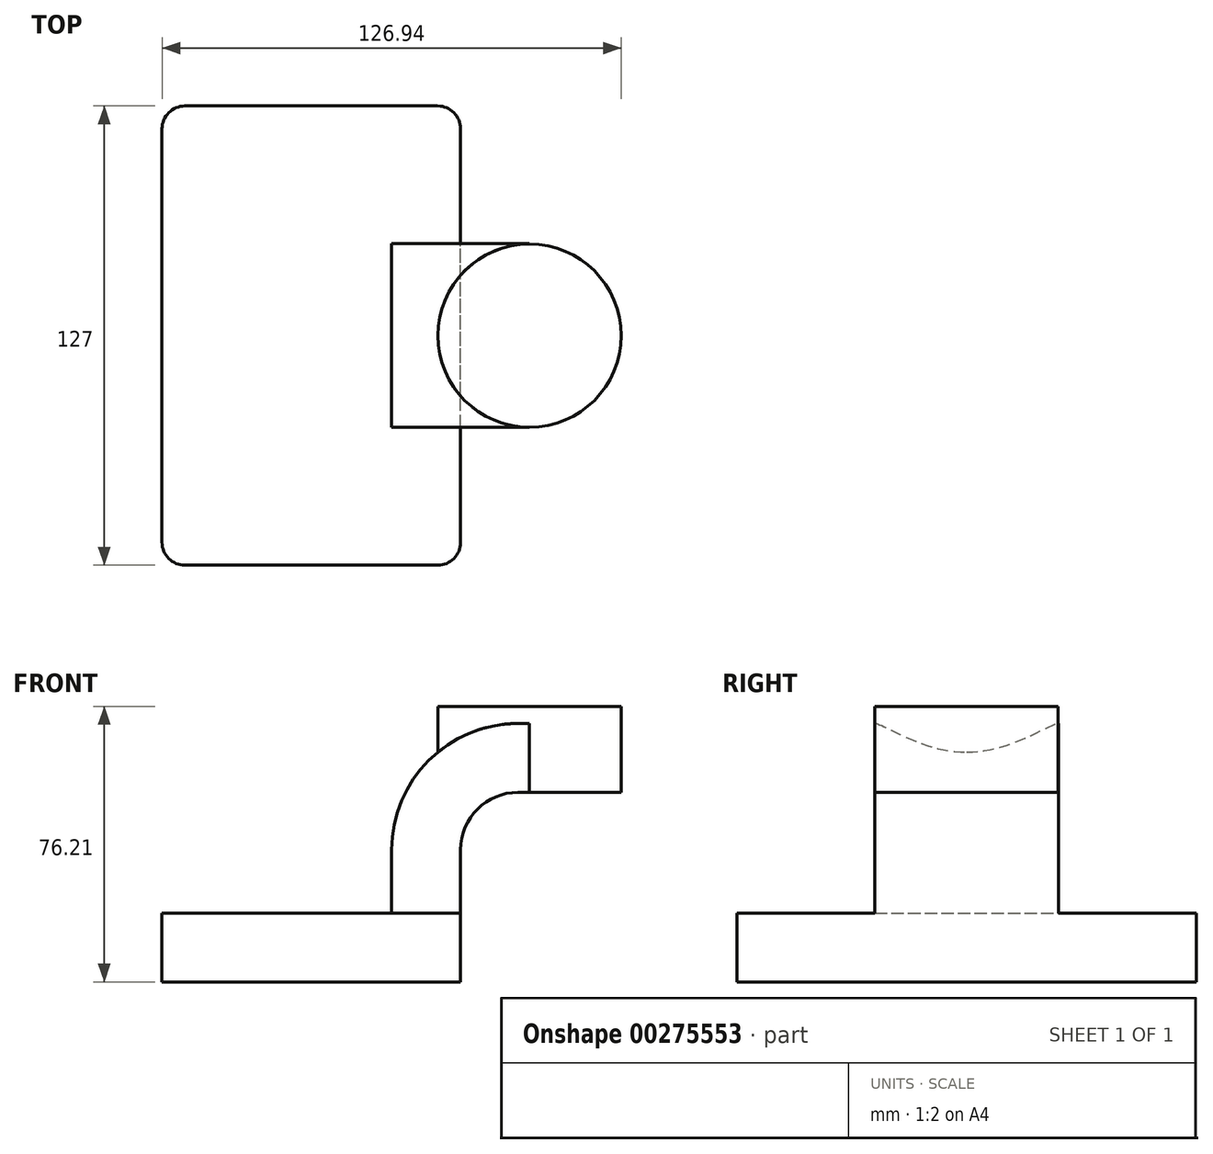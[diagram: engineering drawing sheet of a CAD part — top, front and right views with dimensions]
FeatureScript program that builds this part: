
annotation { "Feature Type Name" : "Feature", "Feature Type Description" : "" }
export const myFeature = defineFeature(function(context is Context, id is Id, definition is map)
    precondition{}
    {
        {
            var Q0;
            Q0=qCreatedBy(makeId("Front.planeOp"),FACE);
            var sketch = newSketch(context, id + "F0", { "sketchPlane" : qUnion([Q0])});
            skLineSegment(sketch, "E0.bottom", {"start": v(41.28, -9.52) * mm, "end": v(-41.28, -9.53) * mm});
            skLineSegment(sketch, "E0.top", {"start": v(41.28, 9.53) * mm, "end": v(-41.28, 9.53) * mm});
            skLineSegment(sketch, "E0.left", {"start": v(41.28, -9.52) * mm, "end": v(41.28, 9.53) * mm});
            skLineSegment(sketch, "E0.right", {"start": v(-41.27, -9.53) * mm, "end": v(-41.28, 9.53) * mm});
            skPoint(sketch, "E0.middle", {"position": v(0, 0) * mm});
            skLineSegment(sketch, "E1.bottom", {"start": v(111.12, 38.1) * mm, "end": v(60.32, 38.1) * mm});
            skLineSegment(sketch, "E1.top", {"start": v(111.12, 66.68) * mm, "end": v(60.32, 66.68) * mm});
            skLineSegment(sketch, "E1.left", {"start": v(111.12, 38.1) * mm, "end": v(111.12, 66.68) * mm});
            skLineSegment(sketch, "E1.right", {"start": v(60.32, 38.1) * mm, "end": v(60.32, 66.68) * mm});
            skPoint(sketch, "E1.middle", {"position": v(85.72, 52.39) * mm});
            skLineSegment(sketch, "E2", {"start": v(41.27, 9.53) * mm, "end": v(41.27, 27) * mm});
            skArc(sketch, "E3", {"start": v(41.27, 27) * mm, "mid": v(45.92, 38.23) * mm, "end": v(57.15, 42.88) * mm});
            skLineSegment(sketch, "E4", {"start": v(57.15, 42.88) * mm, "end": v(85.67, 42.88) * mm});
            skLineSegment(sketch, "E5.0", {"start": v(57.15, 61.93) * mm, "end": v(85.58, 61.93) * mm});
            skArc(sketch, "E5.1", {"start": v(22.23, 27) * mm, "mid": v(32.45, 51.7) * mm, "end": v(57.15, 61.93) * mm});
            skLineSegment(sketch, "E5.2", {"start": v(22.22, 9.53) * mm, "end": v(22.22, 27) * mm});
            skLineSegment(sketch, "E6", {"start": v(85.67, 38.1) * mm, "end": v(85.67, 66.68) * mm});
            skPoint(sketch, "E6.startSnap0", {"position": v(85.72, 38.1) * mm});
            skFitSpline(sketch, "E7", {"points": [v(-41.28, 9.53) * mm, v(57.15, 61.93) * mm], "startDerivative": vector(65.3, 92.3) * mm, "endDerivative": vector(109.77, -5.41) * mm});
            skSolve(sketch);
        }
        {
            var Q0;
            Q0=makeQuery(id+"F0.imprint","IMPRINT",FACE,{"disambiguationData":[TD([[makeQuery(id+"F0.imprint","IMPRINT",EDGE,{"derivedFrom":sQuery(id+"F0.wireOp",EDGE,"E0.bottom")}),-1.0]])]});
            extrude(context, id + "F1", {"entities" : qUnion([Q0]), "endBound" : BoundingType.SYMMETRIC, "depth" : 127 * mm});
        }
        {
            var Q0;
            {var subQ2=sQuery(id+"F0.wireOp",EDGE,"E2");Q0=makeQuery(id+"F0.imprint","IMPRINT",FACE,{"disambiguationData":[TD([[makeQuery(id+"F0.imprint","IMPRINT",EDGE,{"derivedFrom":subQ2}),1.0]])]});}
            extrude(context, id + "F2", {"entities" : qUnion([Q0]), "operationType" : NewBodyOperationType.ADD, "endBound" : BoundingType.SYMMETRIC, "depth" : 50.8 * mm});
        }
        {
            var Q0;
            Q0=makeQuery(id+"F0.imprint","IMPRINT",FACE,{"disambiguationData":[TD([[makeQuery(id+"F0.imprint","IMPRINT",EDGE,{"derivedFrom":sQuery(id+"F0.wireOp",EDGE,"E5.1")}),1.0]])]});
            extrude(context, id + "F3", {"entities" : qUnion([Q0]), "operationType" : NewBodyOperationType.ADD, "endBound" : BoundingType.SYMMETRIC, "depth" : 15.88 * mm});
        }
        {
            var Q0;
            {var subQ3=sQuery(id+"F0.wireOp",EDGE,"E1.right");var subQ5=sQuery(id+"F0.wireOp",EDGE,"E1.top");var subQ6=makeQuery(id+"F0.imprint","INTERSECT",VERTEX,{"derivedFrom":[subQ5,subQ3]});Q0=makeQuery(id+"F0.imprint","IMPRINT",FACE,{"disambiguationData":[TD([[makeQuery(id+"F0.imprint","IMPRINT",EDGE,{"disambiguationData":[TD([[subQ6,1.0]])],"derivedFrom":subQ5}),1.0]])]});}
            var Q1;
            Q1=sQuery(id+"F0.wireOp",EDGE,"E1.right");
            revolve(context, id + "F4", {"operationType" : NewBodyOperationType.ADD, "entities" : qUnion([Q0]), "axis" : qUnion([Q1]), "revolveType" : RevolveType.FULL});
        }
        {
            var Q0;
            Q0=makeQuery(id+"F1.opExtrude","CAP_EDGE",EDGE,{"disambiguationData":[OSD([sQuery(id+"F0.wireOp",EDGE,"E0.right")])],"isStart":false});
            var Q1;
            Q1=makeQuery(id+"F1.opExtrude","CAP_EDGE",EDGE,{"disambiguationData":[OSD([sQuery(id+"F0.wireOp",EDGE,"E0.left")])],"isStart":false});
            var Q2;
            Q2=makeQuery(id+"F1.opExtrude","CAP_EDGE",EDGE,{"disambiguationData":[OSD([sQuery(id+"F0.wireOp",EDGE,"E0.left")])],"isStart":true});
            var Q3;
            Q3=makeQuery(id+"F1.opExtrude","CAP_EDGE",EDGE,{"disambiguationData":[OSD([sQuery(id+"F0.wireOp",EDGE,"E0.right")])],"isStart":true});
            fillet(context, id + "F5", {"entities" : qUnion([Q0, Q1, Q2, Q3]), "radius" : 6.35 * mm, "tangentPropagation" : true, "allowEdgeOverflow" : false});
        }
    });
